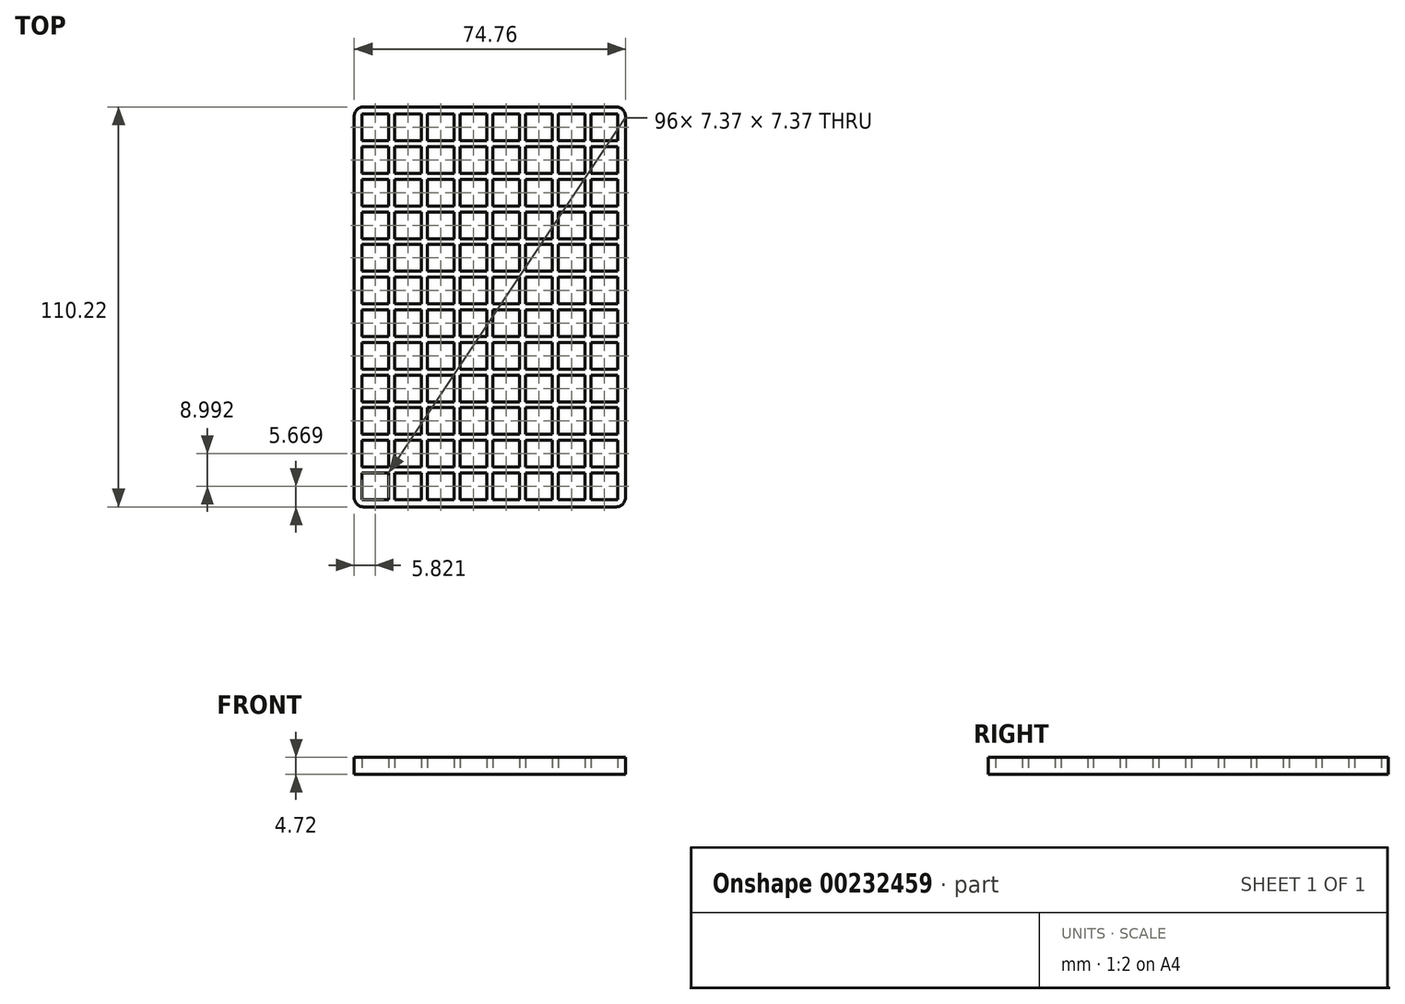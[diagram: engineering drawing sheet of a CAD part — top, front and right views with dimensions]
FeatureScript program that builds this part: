
annotation { "Feature Type Name" : "Feature", "Feature Type Description" : "" }
export const myFeature = defineFeature(function(context is Context, id is Id, definition is map)
    precondition{}
    {
        {
            var Q0;
            Q0=qCreatedBy(makeId("Top.planeOp"),FACE);
            var sketch = newSketch(context, id + "F0", { "sketchPlane" : qUnion([Q0])});
            skLineSegment(sketch, "E0.bottom", {"start": v(-37.38, 55.1) * mm, "end": v(37.38, 55.1) * mm});
            skLineSegment(sketch, "E0.top", {"start": v(-37.38, -55.1) * mm, "end": v(37.38, -55.1) * mm});
            skLineSegment(sketch, "E0.left", {"start": v(-37.38, 55.1) * mm, "end": v(-37.38, -55.1) * mm});
            skLineSegment(sketch, "E0.right", {"start": v(37.38, 55.1) * mm, "end": v(37.38, -55.1) * mm});
            skLineSegment(sketch, "E1.bottom", {"start": v(-35.24, 53.15) * mm, "end": v(-27.88, 53.15) * mm});
            skLineSegment(sketch, "E1.top", {"start": v(-35.24, 45.78) * mm, "end": v(-27.88, 45.78) * mm});
            skLineSegment(sketch, "E1.left", {"start": v(-35.24, 53.15) * mm, "end": v(-35.24, 45.78) * mm});
            skLineSegment(sketch, "E1.right", {"start": v(-27.88, 53.15) * mm, "end": v(-27.88, 45.78) * mm});
            skLineSegment(sketch, "E2.1.0.0", {"start": v(-18.86, 53.15) * mm, "end": v(-18.86, 45.78) * mm});
            skLineSegment(sketch, "E2.1.0.1", {"start": v(-26.23, 45.78) * mm, "end": v(-18.86, 45.78) * mm});
            skLineSegment(sketch, "E2.1.0.2", {"start": v(-26.23, 53.15) * mm, "end": v(-26.23, 45.78) * mm});
            skLineSegment(sketch, "E2.1.0.3", {"start": v(-26.23, 53.15) * mm, "end": v(-18.86, 53.15) * mm});
            skLineSegment(sketch, "E2.2.0.0", {"start": v(-9.84, 53.15) * mm, "end": v(-9.84, 45.78) * mm});
            skLineSegment(sketch, "E2.2.0.1", {"start": v(-17.2, 45.78) * mm, "end": v(-9.84, 45.78) * mm});
            skLineSegment(sketch, "E2.2.0.2", {"start": v(-17.2, 53.15) * mm, "end": v(-17.2, 45.78) * mm});
            skLineSegment(sketch, "E2.2.0.3", {"start": v(-17.2, 53.15) * mm, "end": v(-9.84, 53.15) * mm});
            skLineSegment(sketch, "E3.1.0.0", {"start": v(0.83, 53.15) * mm, "end": v(0.83, 45.78) * mm});
            skLineSegment(sketch, "E3.1.0.1", {"start": v(0.83, 45.78) * mm, "end": v(8.2, 45.78) * mm});
            skLineSegment(sketch, "E3.1.0.2", {"start": v(-0.83, 53.15) * mm, "end": v(-0.83, 45.78) * mm});
            skLineSegment(sketch, "E3.1.0.3", {"start": v(0.83, 53.15) * mm, "end": v(8.2, 53.15) * mm});
            skLineSegment(sketch, "E3.1.0.4", {"start": v(17.2, 53.15) * mm, "end": v(17.2, 45.78) * mm});
            skLineSegment(sketch, "E3.1.0.5", {"start": v(-8.2, 53.15) * mm, "end": v(-8.2, 45.78) * mm});
            skLineSegment(sketch, "E3.1.0.6", {"start": v(-8.2, 45.78) * mm, "end": v(-0.83, 45.78) * mm});
            skLineSegment(sketch, "E3.1.0.7", {"start": v(9.84, 53.15) * mm, "end": v(17.2, 53.15) * mm});
            skLineSegment(sketch, "E3.1.0.8", {"start": v(9.84, 45.78) * mm, "end": v(17.2, 45.78) * mm});
            skLineSegment(sketch, "E3.1.0.9", {"start": v(8.2, 53.15) * mm, "end": v(8.2, 45.78) * mm});
            skLineSegment(sketch, "E3.1.0.10", {"start": v(-8.2, 53.15) * mm, "end": v(-0.83, 53.15) * mm});
            skLineSegment(sketch, "E3.1.0.11", {"start": v(9.84, 53.15) * mm, "end": v(9.84, 45.78) * mm});
            skLineSegment(sketch, "E3.2.0.0", {"start": v(27.88, 53.15) * mm, "end": v(27.88, 45.78) * mm});
            skLineSegment(sketch, "E3.2.0.1", {"start": v(27.88, 45.78) * mm, "end": v(35.24, 45.78) * mm});
            skLineSegment(sketch, "E3.2.0.2", {"start": v(26.23, 53.15) * mm, "end": v(26.23, 45.78) * mm});
            skLineSegment(sketch, "E3.2.0.3", {"start": v(27.88, 53.15) * mm, "end": v(35.24, 53.15) * mm});
            skLineSegment(sketch, "E3.2.0.5", {"start": v(18.86, 53.15) * mm, "end": v(18.86, 45.78) * mm});
            skLineSegment(sketch, "E3.2.0.6", {"start": v(18.86, 45.78) * mm, "end": v(26.23, 45.78) * mm});
            skLineSegment(sketch, "E3.2.0.9", {"start": v(35.24, 53.15) * mm, "end": v(35.24, 45.78) * mm});
            skLineSegment(sketch, "E3.2.0.10", {"start": v(18.86, 53.15) * mm, "end": v(26.23, 53.15) * mm});
            skLineSegment(sketch, "E4.1.0.0", {"start": v(-8.2, 44.16) * mm, "end": v(-0.83, 44.16) * mm});
            skLineSegment(sketch, "E4.1.0.1", {"start": v(0.83, 44.16) * mm, "end": v(8.2, 44.16) * mm});
            skLineSegment(sketch, "E4.1.0.2", {"start": v(18.86, 44.16) * mm, "end": v(26.23, 44.16) * mm});
            skLineSegment(sketch, "E4.1.0.3", {"start": v(-17.2, 36.8) * mm, "end": v(-9.84, 36.8) * mm});
            skLineSegment(sketch, "E4.1.0.4", {"start": v(8.2, 44.16) * mm, "end": v(8.2, 36.8) * mm});
            skLineSegment(sketch, "E4.1.0.5", {"start": v(-35.24, 36.8) * mm, "end": v(-27.88, 36.8) * mm});
            skLineSegment(sketch, "E4.1.0.6", {"start": v(-17.2, 44.16) * mm, "end": v(-17.2, 36.8) * mm});
            skLineSegment(sketch, "E4.1.0.7", {"start": v(-17.2, 44.16) * mm, "end": v(-9.84, 44.16) * mm});
            skLineSegment(sketch, "E4.1.0.8", {"start": v(-0.83, 44.16) * mm, "end": v(-0.83, 36.8) * mm});
            skLineSegment(sketch, "E4.1.0.9", {"start": v(-35.24, 44.16) * mm, "end": v(-27.88, 44.16) * mm});
            skLineSegment(sketch, "E4.1.0.10", {"start": v(27.88, 44.16) * mm, "end": v(35.24, 44.16) * mm});
            skLineSegment(sketch, "E4.1.0.11", {"start": v(-8.2, 36.8) * mm, "end": v(-0.83, 36.8) * mm});
            skLineSegment(sketch, "E4.1.0.12", {"start": v(-35.24, 44.16) * mm, "end": v(-35.24, 36.8) * mm});
            skLineSegment(sketch, "E4.1.0.13", {"start": v(-27.88, 44.16) * mm, "end": v(-27.88, 36.8) * mm});
            skLineSegment(sketch, "E4.1.0.14", {"start": v(0.83, 36.8) * mm, "end": v(8.2, 36.8) * mm});
            skLineSegment(sketch, "E4.1.0.15", {"start": v(18.86, 36.8) * mm, "end": v(26.23, 36.8) * mm});
            skLineSegment(sketch, "E4.1.0.16", {"start": v(-18.86, 44.16) * mm, "end": v(-18.86, 36.8) * mm});
            skLineSegment(sketch, "E4.1.0.17", {"start": v(-26.23, 36.8) * mm, "end": v(-18.86, 36.8) * mm});
            skLineSegment(sketch, "E4.1.0.18", {"start": v(-26.23, 44.16) * mm, "end": v(-26.23, 36.8) * mm});
            skLineSegment(sketch, "E4.1.0.19", {"start": v(-26.23, 44.16) * mm, "end": v(-18.86, 44.16) * mm});
            skLineSegment(sketch, "E4.1.0.20", {"start": v(-9.84, 44.16) * mm, "end": v(-9.84, 36.8) * mm});
            skLineSegment(sketch, "E4.1.0.21", {"start": v(9.84, 44.16) * mm, "end": v(9.84, 36.8) * mm});
            skLineSegment(sketch, "E4.1.0.22", {"start": v(9.84, 44.16) * mm, "end": v(17.2, 44.16) * mm});
            skLineSegment(sketch, "E4.1.0.23", {"start": v(17.2, 44.16) * mm, "end": v(17.2, 36.8) * mm});
            skLineSegment(sketch, "E4.1.0.24", {"start": v(27.88, 36.8) * mm, "end": v(35.24, 36.8) * mm});
            skLineSegment(sketch, "E4.1.0.25", {"start": v(0.83, 44.16) * mm, "end": v(0.83, 36.8) * mm});
            skLineSegment(sketch, "E4.1.0.26", {"start": v(18.86, 44.16) * mm, "end": v(18.86, 36.8) * mm});
            skLineSegment(sketch, "E4.1.0.27", {"start": v(27.88, 44.16) * mm, "end": v(27.88, 36.8) * mm});
            skLineSegment(sketch, "E4.1.0.28", {"start": v(9.84, 36.8) * mm, "end": v(17.2, 36.8) * mm});
            skLineSegment(sketch, "E4.1.0.29", {"start": v(26.23, 44.16) * mm, "end": v(26.23, 36.8) * mm});
            skLineSegment(sketch, "E4.1.0.30", {"start": v(-8.2, 44.16) * mm, "end": v(-8.2, 36.8) * mm});
            skLineSegment(sketch, "E4.1.0.31", {"start": v(35.24, 44.16) * mm, "end": v(35.24, 36.8) * mm});
            skLineSegment(sketch, "E4.2.0.0", {"start": v(-8.2, 35.17) * mm, "end": v(-0.83, 35.17) * mm});
            skLineSegment(sketch, "E4.2.0.1", {"start": v(0.83, 35.17) * mm, "end": v(8.2, 35.17) * mm});
            skLineSegment(sketch, "E4.2.0.2", {"start": v(18.86, 35.17) * mm, "end": v(26.23, 35.17) * mm});
            skLineSegment(sketch, "E4.2.0.3", {"start": v(-17.2, 27.8) * mm, "end": v(-9.84, 27.8) * mm});
            skLineSegment(sketch, "E4.2.0.4", {"start": v(8.2, 35.17) * mm, "end": v(8.2, 27.8) * mm});
            skLineSegment(sketch, "E4.2.0.5", {"start": v(-35.24, 27.8) * mm, "end": v(-27.88, 27.8) * mm});
            skLineSegment(sketch, "E4.2.0.6", {"start": v(-17.2, 35.17) * mm, "end": v(-17.2, 27.8) * mm});
            skLineSegment(sketch, "E4.2.0.7", {"start": v(-17.2, 35.17) * mm, "end": v(-9.84, 35.17) * mm});
            skLineSegment(sketch, "E4.2.0.8", {"start": v(-0.83, 35.17) * mm, "end": v(-0.83, 27.8) * mm});
            skLineSegment(sketch, "E4.2.0.9", {"start": v(-35.24, 35.17) * mm, "end": v(-27.88, 35.17) * mm});
            skLineSegment(sketch, "E4.2.0.10", {"start": v(27.88, 35.17) * mm, "end": v(35.24, 35.17) * mm});
            skLineSegment(sketch, "E4.2.0.11", {"start": v(-8.2, 27.8) * mm, "end": v(-0.83, 27.8) * mm});
            skLineSegment(sketch, "E4.2.0.12", {"start": v(-35.24, 35.17) * mm, "end": v(-35.24, 27.8) * mm});
            skLineSegment(sketch, "E4.2.0.13", {"start": v(-27.88, 35.17) * mm, "end": v(-27.88, 27.8) * mm});
            skLineSegment(sketch, "E4.2.0.14", {"start": v(0.83, 27.8) * mm, "end": v(8.2, 27.8) * mm});
            skLineSegment(sketch, "E4.2.0.15", {"start": v(18.86, 27.8) * mm, "end": v(26.23, 27.8) * mm});
            skLineSegment(sketch, "E4.2.0.16", {"start": v(-18.86, 35.17) * mm, "end": v(-18.86, 27.8) * mm});
            skLineSegment(sketch, "E4.2.0.17", {"start": v(-26.23, 27.8) * mm, "end": v(-18.86, 27.8) * mm});
            skLineSegment(sketch, "E4.2.0.18", {"start": v(-26.23, 35.17) * mm, "end": v(-26.23, 27.8) * mm});
            skLineSegment(sketch, "E4.2.0.19", {"start": v(-26.23, 35.17) * mm, "end": v(-18.86, 35.17) * mm});
            skLineSegment(sketch, "E4.2.0.20", {"start": v(-9.84, 35.17) * mm, "end": v(-9.84, 27.8) * mm});
            skLineSegment(sketch, "E4.2.0.21", {"start": v(9.84, 35.17) * mm, "end": v(9.84, 27.8) * mm});
            skLineSegment(sketch, "E4.2.0.22", {"start": v(9.84, 35.17) * mm, "end": v(17.2, 35.17) * mm});
            skLineSegment(sketch, "E4.2.0.23", {"start": v(17.2, 35.17) * mm, "end": v(17.2, 27.8) * mm});
            skLineSegment(sketch, "E4.2.0.24", {"start": v(27.88, 27.8) * mm, "end": v(35.24, 27.8) * mm});
            skLineSegment(sketch, "E4.2.0.25", {"start": v(0.83, 35.17) * mm, "end": v(0.83, 27.8) * mm});
            skLineSegment(sketch, "E4.2.0.26", {"start": v(18.86, 35.17) * mm, "end": v(18.86, 27.8) * mm});
            skLineSegment(sketch, "E4.2.0.27", {"start": v(27.88, 35.17) * mm, "end": v(27.88, 27.8) * mm});
            skLineSegment(sketch, "E4.2.0.28", {"start": v(9.84, 27.8) * mm, "end": v(17.2, 27.8) * mm});
            skLineSegment(sketch, "E4.2.0.29", {"start": v(26.23, 35.17) * mm, "end": v(26.23, 27.8) * mm});
            skLineSegment(sketch, "E4.2.0.30", {"start": v(-8.2, 35.17) * mm, "end": v(-8.2, 27.8) * mm});
            skLineSegment(sketch, "E4.2.0.31", {"start": v(35.24, 35.17) * mm, "end": v(35.24, 27.8) * mm});
            skLineSegment(sketch, "E4.direction1", {"start": v(-35.24, 45.78) * mm, "end": v(-35.24, 36.8) * mm, "construction": true});
            skLineSegment(sketch, "E5.0.3.0", {"start": v(-8.2, 26.17) * mm, "end": v(-0.83, 26.17) * mm});
            skLineSegment(sketch, "E5.3.3.0", {"start": v(0.83, 26.17) * mm, "end": v(8.2, 26.17) * mm});
            skLineSegment(sketch, "E5.6.3.0", {"start": v(18.86, 26.17) * mm, "end": v(26.23, 26.17) * mm});
            skLineSegment(sketch, "E5.9.3.0", {"start": v(-17.2, 18.8) * mm, "end": v(-9.84, 18.8) * mm});
            skLineSegment(sketch, "E5.12.3.0", {"start": v(8.2, 26.17) * mm, "end": v(8.2, 18.8) * mm});
            skLineSegment(sketch, "E5.15.3.0", {"start": v(-35.24, 18.8) * mm, "end": v(-27.88, 18.8) * mm});
            skLineSegment(sketch, "E5.18.3.0", {"start": v(-17.2, 26.17) * mm, "end": v(-17.2, 18.8) * mm});
            skLineSegment(sketch, "E5.21.3.0", {"start": v(-17.2, 26.17) * mm, "end": v(-9.84, 26.17) * mm});
            skLineSegment(sketch, "E5.24.3.0", {"start": v(-0.83, 26.17) * mm, "end": v(-0.83, 18.8) * mm});
            skLineSegment(sketch, "E5.27.3.0", {"start": v(-35.24, 26.17) * mm, "end": v(-27.88, 26.17) * mm});
            skLineSegment(sketch, "E5.30.3.0", {"start": v(27.88, 26.17) * mm, "end": v(35.24, 26.17) * mm});
            skLineSegment(sketch, "E5.33.3.0", {"start": v(-8.2, 18.8) * mm, "end": v(-0.83, 18.8) * mm});
            skLineSegment(sketch, "E5.36.3.0", {"start": v(-35.24, 26.17) * mm, "end": v(-35.24, 18.8) * mm});
            skLineSegment(sketch, "E5.39.3.0", {"start": v(-27.88, 26.17) * mm, "end": v(-27.88, 18.8) * mm});
            skLineSegment(sketch, "E5.42.3.0", {"start": v(0.83, 18.8) * mm, "end": v(8.2, 18.8) * mm});
            skLineSegment(sketch, "E5.45.3.0", {"start": v(18.86, 18.8) * mm, "end": v(26.23, 18.8) * mm});
            skLineSegment(sketch, "E5.48.3.0", {"start": v(-18.86, 26.17) * mm, "end": v(-18.86, 18.8) * mm});
            skLineSegment(sketch, "E5.51.3.0", {"start": v(-26.23, 18.8) * mm, "end": v(-18.86, 18.8) * mm});
            skLineSegment(sketch, "E5.54.3.0", {"start": v(-26.23, 26.17) * mm, "end": v(-26.23, 18.8) * mm});
            skLineSegment(sketch, "E5.57.3.0", {"start": v(-26.23, 26.17) * mm, "end": v(-18.86, 26.17) * mm});
            skLineSegment(sketch, "E5.60.3.0", {"start": v(-9.84, 26.17) * mm, "end": v(-9.84, 18.8) * mm});
            skLineSegment(sketch, "E5.63.3.0", {"start": v(9.84, 26.17) * mm, "end": v(9.84, 18.8) * mm});
            skLineSegment(sketch, "E5.66.3.0", {"start": v(9.84, 26.17) * mm, "end": v(17.2, 26.17) * mm});
            skLineSegment(sketch, "E5.69.3.0", {"start": v(17.2, 26.17) * mm, "end": v(17.2, 18.8) * mm});
            skLineSegment(sketch, "E5.72.3.0", {"start": v(27.88, 18.8) * mm, "end": v(35.24, 18.8) * mm});
            skLineSegment(sketch, "E5.75.3.0", {"start": v(0.83, 26.17) * mm, "end": v(0.83, 18.8) * mm});
            skLineSegment(sketch, "E5.78.3.0", {"start": v(18.86, 26.17) * mm, "end": v(18.86, 18.8) * mm});
            skLineSegment(sketch, "E5.81.3.0", {"start": v(27.88, 26.17) * mm, "end": v(27.88, 18.8) * mm});
            skLineSegment(sketch, "E5.84.3.0", {"start": v(9.84, 18.8) * mm, "end": v(17.2, 18.8) * mm});
            skLineSegment(sketch, "E5.87.3.0", {"start": v(26.23, 26.17) * mm, "end": v(26.23, 18.8) * mm});
            skLineSegment(sketch, "E5.90.3.0", {"start": v(-8.2, 26.17) * mm, "end": v(-8.2, 18.8) * mm});
            skLineSegment(sketch, "E5.93.3.0", {"start": v(35.24, 26.17) * mm, "end": v(35.24, 18.8) * mm});
            skLineSegment(sketch, "E5.0.4.0", {"start": v(-8.2, 17.18) * mm, "end": v(-0.83, 17.18) * mm});
            skLineSegment(sketch, "E5.3.4.0", {"start": v(0.83, 17.18) * mm, "end": v(8.2, 17.18) * mm});
            skLineSegment(sketch, "E5.6.4.0", {"start": v(18.86, 17.18) * mm, "end": v(26.23, 17.18) * mm});
            skLineSegment(sketch, "E5.9.4.0", {"start": v(-17.2, 9.82) * mm, "end": v(-9.84, 9.82) * mm});
            skLineSegment(sketch, "E5.12.4.0", {"start": v(8.2, 17.18) * mm, "end": v(8.2, 9.82) * mm});
            skLineSegment(sketch, "E5.15.4.0", {"start": v(-35.24, 9.82) * mm, "end": v(-27.88, 9.82) * mm});
            skLineSegment(sketch, "E5.18.4.0", {"start": v(-17.2, 17.18) * mm, "end": v(-17.2, 9.82) * mm});
            skLineSegment(sketch, "E5.21.4.0", {"start": v(-17.2, 17.18) * mm, "end": v(-9.84, 17.18) * mm});
            skLineSegment(sketch, "E5.24.4.0", {"start": v(-0.83, 17.18) * mm, "end": v(-0.83, 9.82) * mm});
            skLineSegment(sketch, "E5.27.4.0", {"start": v(-35.24, 17.18) * mm, "end": v(-27.88, 17.18) * mm});
            skLineSegment(sketch, "E5.30.4.0", {"start": v(27.88, 17.18) * mm, "end": v(35.24, 17.18) * mm});
            skLineSegment(sketch, "E5.33.4.0", {"start": v(-8.2, 9.82) * mm, "end": v(-0.83, 9.82) * mm});
            skLineSegment(sketch, "E5.36.4.0", {"start": v(-35.24, 17.18) * mm, "end": v(-35.24, 9.82) * mm});
            skLineSegment(sketch, "E5.39.4.0", {"start": v(-27.88, 17.18) * mm, "end": v(-27.88, 9.82) * mm});
            skLineSegment(sketch, "E5.42.4.0", {"start": v(0.83, 9.82) * mm, "end": v(8.2, 9.82) * mm});
            skLineSegment(sketch, "E5.45.4.0", {"start": v(18.86, 9.82) * mm, "end": v(26.23, 9.82) * mm});
            skLineSegment(sketch, "E5.48.4.0", {"start": v(-18.86, 17.18) * mm, "end": v(-18.86, 9.82) * mm});
            skLineSegment(sketch, "E5.51.4.0", {"start": v(-26.23, 9.82) * mm, "end": v(-18.86, 9.82) * mm});
            skLineSegment(sketch, "E5.54.4.0", {"start": v(-26.23, 17.18) * mm, "end": v(-26.23, 9.82) * mm});
            skLineSegment(sketch, "E5.57.4.0", {"start": v(-26.23, 17.18) * mm, "end": v(-18.86, 17.18) * mm});
            skLineSegment(sketch, "E5.60.4.0", {"start": v(-9.84, 17.18) * mm, "end": v(-9.84, 9.82) * mm});
            skLineSegment(sketch, "E5.63.4.0", {"start": v(9.84, 17.18) * mm, "end": v(9.84, 9.82) * mm});
            skLineSegment(sketch, "E5.66.4.0", {"start": v(9.84, 17.18) * mm, "end": v(17.2, 17.18) * mm});
            skLineSegment(sketch, "E5.69.4.0", {"start": v(17.2, 17.18) * mm, "end": v(17.2, 9.82) * mm});
            skLineSegment(sketch, "E5.72.4.0", {"start": v(27.88, 9.82) * mm, "end": v(35.24, 9.82) * mm});
            skLineSegment(sketch, "E5.75.4.0", {"start": v(0.83, 17.18) * mm, "end": v(0.83, 9.82) * mm});
            skLineSegment(sketch, "E5.78.4.0", {"start": v(18.86, 17.18) * mm, "end": v(18.86, 9.82) * mm});
            skLineSegment(sketch, "E5.81.4.0", {"start": v(27.88, 17.18) * mm, "end": v(27.88, 9.82) * mm});
            skLineSegment(sketch, "E5.84.4.0", {"start": v(9.84, 9.82) * mm, "end": v(17.2, 9.82) * mm});
            skLineSegment(sketch, "E5.87.4.0", {"start": v(26.23, 17.18) * mm, "end": v(26.23, 9.82) * mm});
            skLineSegment(sketch, "E5.90.4.0", {"start": v(-8.2, 17.18) * mm, "end": v(-8.2, 9.82) * mm});
            skLineSegment(sketch, "E5.93.4.0", {"start": v(35.24, 17.18) * mm, "end": v(35.24, 9.82) * mm});
            skLineSegment(sketch, "E5.0.5.0", {"start": v(-8.2, 8.2) * mm, "end": v(-0.83, 8.2) * mm});
            skLineSegment(sketch, "E5.3.5.0", {"start": v(0.83, 8.2) * mm, "end": v(8.2, 8.2) * mm});
            skLineSegment(sketch, "E5.6.5.0", {"start": v(18.86, 8.2) * mm, "end": v(26.23, 8.2) * mm});
            skLineSegment(sketch, "E5.9.5.0", {"start": v(-17.2, 0.83) * mm, "end": v(-9.84, 0.83) * mm});
            skLineSegment(sketch, "E5.12.5.0", {"start": v(8.2, 8.2) * mm, "end": v(8.2, 0.83) * mm});
            skLineSegment(sketch, "E5.15.5.0", {"start": v(-35.24, 0.83) * mm, "end": v(-27.88, 0.83) * mm});
            skLineSegment(sketch, "E5.18.5.0", {"start": v(-17.2, 8.2) * mm, "end": v(-17.2, 0.83) * mm});
            skLineSegment(sketch, "E5.21.5.0", {"start": v(-17.2, 8.2) * mm, "end": v(-9.84, 8.2) * mm});
            skLineSegment(sketch, "E5.24.5.0", {"start": v(-0.83, 8.2) * mm, "end": v(-0.83, 0.83) * mm});
            skLineSegment(sketch, "E5.27.5.0", {"start": v(-35.24, 8.2) * mm, "end": v(-27.88, 8.2) * mm});
            skLineSegment(sketch, "E5.30.5.0", {"start": v(27.88, 8.2) * mm, "end": v(35.24, 8.2) * mm});
            skLineSegment(sketch, "E5.33.5.0", {"start": v(-8.2, 0.83) * mm, "end": v(-0.83, 0.83) * mm});
            skLineSegment(sketch, "E5.36.5.0", {"start": v(-35.24, 8.2) * mm, "end": v(-35.24, 0.83) * mm});
            skLineSegment(sketch, "E5.39.5.0", {"start": v(-27.88, 8.2) * mm, "end": v(-27.88, 0.83) * mm});
            skLineSegment(sketch, "E5.42.5.0", {"start": v(0.83, 0.83) * mm, "end": v(8.2, 0.83) * mm});
            skLineSegment(sketch, "E5.45.5.0", {"start": v(18.86, 0.83) * mm, "end": v(26.23, 0.83) * mm});
            skLineSegment(sketch, "E5.48.5.0", {"start": v(-18.86, 8.2) * mm, "end": v(-18.86, 0.83) * mm});
            skLineSegment(sketch, "E5.51.5.0", {"start": v(-26.23, 0.83) * mm, "end": v(-18.86, 0.83) * mm});
            skLineSegment(sketch, "E5.54.5.0", {"start": v(-26.23, 8.2) * mm, "end": v(-26.23, 0.83) * mm});
            skLineSegment(sketch, "E5.57.5.0", {"start": v(-26.23, 8.2) * mm, "end": v(-18.86, 8.2) * mm});
            skLineSegment(sketch, "E5.60.5.0", {"start": v(-9.84, 8.2) * mm, "end": v(-9.84, 0.83) * mm});
            skLineSegment(sketch, "E5.63.5.0", {"start": v(9.84, 8.2) * mm, "end": v(9.84, 0.83) * mm});
            skLineSegment(sketch, "E5.66.5.0", {"start": v(9.84, 8.2) * mm, "end": v(17.2, 8.2) * mm});
            skLineSegment(sketch, "E5.69.5.0", {"start": v(17.2, 8.2) * mm, "end": v(17.2, 0.83) * mm});
            skLineSegment(sketch, "E5.72.5.0", {"start": v(27.88, 0.83) * mm, "end": v(35.24, 0.83) * mm});
            skLineSegment(sketch, "E5.75.5.0", {"start": v(0.83, 8.2) * mm, "end": v(0.83, 0.83) * mm});
            skLineSegment(sketch, "E5.78.5.0", {"start": v(18.86, 8.2) * mm, "end": v(18.86, 0.83) * mm});
            skLineSegment(sketch, "E5.81.5.0", {"start": v(27.88, 8.2) * mm, "end": v(27.88, 0.83) * mm});
            skLineSegment(sketch, "E5.84.5.0", {"start": v(9.84, 0.83) * mm, "end": v(17.2, 0.83) * mm});
            skLineSegment(sketch, "E5.87.5.0", {"start": v(26.23, 8.2) * mm, "end": v(26.23, 0.83) * mm});
            skLineSegment(sketch, "E5.90.5.0", {"start": v(-8.2, 8.2) * mm, "end": v(-8.2, 0.83) * mm});
            skLineSegment(sketch, "E5.93.5.0", {"start": v(35.24, 8.2) * mm, "end": v(35.24, 0.83) * mm});
            skLineSegment(sketch, "E5.0.6.0", {"start": v(-8.2, -0.8) * mm, "end": v(-0.83, -0.8) * mm});
            skLineSegment(sketch, "E5.3.6.0", {"start": v(0.83, -0.8) * mm, "end": v(8.2, -0.8) * mm});
            skLineSegment(sketch, "E5.6.6.0", {"start": v(18.86, -0.8) * mm, "end": v(26.23, -0.8) * mm});
            skLineSegment(sketch, "E5.9.6.0", {"start": v(-17.2, -8.17) * mm, "end": v(-9.84, -8.17) * mm});
            skLineSegment(sketch, "E5.12.6.0", {"start": v(8.2, -0.8) * mm, "end": v(8.2, -8.17) * mm});
            skLineSegment(sketch, "E5.15.6.0", {"start": v(-35.24, -8.17) * mm, "end": v(-27.88, -8.17) * mm});
            skLineSegment(sketch, "E5.18.6.0", {"start": v(-17.2, -0.8) * mm, "end": v(-17.2, -8.17) * mm});
            skLineSegment(sketch, "E5.21.6.0", {"start": v(-17.2, -0.8) * mm, "end": v(-9.84, -0.8) * mm});
            skLineSegment(sketch, "E5.24.6.0", {"start": v(-0.83, -0.8) * mm, "end": v(-0.83, -8.17) * mm});
            skLineSegment(sketch, "E5.27.6.0", {"start": v(-35.24, -0.8) * mm, "end": v(-27.88, -0.8) * mm});
            skLineSegment(sketch, "E5.30.6.0", {"start": v(27.88, -0.8) * mm, "end": v(35.24, -0.8) * mm});
            skLineSegment(sketch, "E5.33.6.0", {"start": v(-8.2, -8.17) * mm, "end": v(-0.83, -8.17) * mm});
            skLineSegment(sketch, "E5.36.6.0", {"start": v(-35.24, -0.8) * mm, "end": v(-35.24, -8.17) * mm});
            skLineSegment(sketch, "E5.39.6.0", {"start": v(-27.88, -0.8) * mm, "end": v(-27.88, -8.17) * mm});
            skLineSegment(sketch, "E5.42.6.0", {"start": v(0.83, -8.17) * mm, "end": v(8.2, -8.17) * mm});
            skLineSegment(sketch, "E5.45.6.0", {"start": v(18.86, -8.17) * mm, "end": v(26.23, -8.17) * mm});
            skLineSegment(sketch, "E5.48.6.0", {"start": v(-18.86, -0.8) * mm, "end": v(-18.86, -8.17) * mm});
            skLineSegment(sketch, "E5.51.6.0", {"start": v(-26.23, -8.17) * mm, "end": v(-18.86, -8.17) * mm});
            skLineSegment(sketch, "E5.54.6.0", {"start": v(-26.23, -0.8) * mm, "end": v(-26.23, -8.17) * mm});
            skLineSegment(sketch, "E5.57.6.0", {"start": v(-26.23, -0.8) * mm, "end": v(-18.86, -0.8) * mm});
            skLineSegment(sketch, "E5.60.6.0", {"start": v(-9.84, -0.8) * mm, "end": v(-9.84, -8.17) * mm});
            skLineSegment(sketch, "E5.63.6.0", {"start": v(9.84, -0.8) * mm, "end": v(9.84, -8.17) * mm});
            skLineSegment(sketch, "E5.66.6.0", {"start": v(9.84, -0.8) * mm, "end": v(17.2, -0.8) * mm});
            skLineSegment(sketch, "E5.69.6.0", {"start": v(17.2, -0.8) * mm, "end": v(17.2, -8.17) * mm});
            skLineSegment(sketch, "E5.72.6.0", {"start": v(27.88, -8.17) * mm, "end": v(35.24, -8.17) * mm});
            skLineSegment(sketch, "E5.75.6.0", {"start": v(0.83, -0.8) * mm, "end": v(0.83, -8.17) * mm});
            skLineSegment(sketch, "E5.78.6.0", {"start": v(18.86, -0.8) * mm, "end": v(18.86, -8.17) * mm});
            skLineSegment(sketch, "E5.81.6.0", {"start": v(27.88, -0.8) * mm, "end": v(27.88, -8.17) * mm});
            skLineSegment(sketch, "E5.84.6.0", {"start": v(9.84, -8.17) * mm, "end": v(17.2, -8.17) * mm});
            skLineSegment(sketch, "E5.87.6.0", {"start": v(26.23, -0.8) * mm, "end": v(26.23, -8.17) * mm});
            skLineSegment(sketch, "E5.90.6.0", {"start": v(-8.2, -0.8) * mm, "end": v(-8.2, -8.17) * mm});
            skLineSegment(sketch, "E5.93.6.0", {"start": v(35.24, -0.8) * mm, "end": v(35.24, -8.17) * mm});
            skLineSegment(sketch, "E5.0.7.0", {"start": v(-8.2, -9.8) * mm, "end": v(-0.83, -9.8) * mm});
            skLineSegment(sketch, "E5.3.7.0", {"start": v(0.83, -9.8) * mm, "end": v(8.2, -9.8) * mm});
            skLineSegment(sketch, "E5.6.7.0", {"start": v(18.86, -9.8) * mm, "end": v(26.23, -9.8) * mm});
            skLineSegment(sketch, "E5.9.7.0", {"start": v(-17.2, -17.16) * mm, "end": v(-9.84, -17.16) * mm});
            skLineSegment(sketch, "E5.12.7.0", {"start": v(8.2, -9.8) * mm, "end": v(8.2, -17.16) * mm});
            skLineSegment(sketch, "E5.15.7.0", {"start": v(-35.24, -17.16) * mm, "end": v(-27.88, -17.16) * mm});
            skLineSegment(sketch, "E5.18.7.0", {"start": v(-17.2, -9.8) * mm, "end": v(-17.2, -17.16) * mm});
            skLineSegment(sketch, "E5.21.7.0", {"start": v(-17.2, -9.8) * mm, "end": v(-9.84, -9.8) * mm});
            skLineSegment(sketch, "E5.24.7.0", {"start": v(-0.83, -9.8) * mm, "end": v(-0.83, -17.16) * mm});
            skLineSegment(sketch, "E5.27.7.0", {"start": v(-35.24, -9.8) * mm, "end": v(-27.88, -9.8) * mm});
            skLineSegment(sketch, "E5.30.7.0", {"start": v(27.88, -9.8) * mm, "end": v(35.24, -9.8) * mm});
            skLineSegment(sketch, "E5.33.7.0", {"start": v(-8.2, -17.16) * mm, "end": v(-0.83, -17.16) * mm});
            skLineSegment(sketch, "E5.36.7.0", {"start": v(-35.24, -9.8) * mm, "end": v(-35.24, -17.16) * mm});
            skLineSegment(sketch, "E5.39.7.0", {"start": v(-27.88, -9.8) * mm, "end": v(-27.88, -17.16) * mm});
            skLineSegment(sketch, "E5.42.7.0", {"start": v(0.83, -17.16) * mm, "end": v(8.2, -17.16) * mm});
            skLineSegment(sketch, "E5.45.7.0", {"start": v(18.86, -17.16) * mm, "end": v(26.23, -17.16) * mm});
            skLineSegment(sketch, "E5.48.7.0", {"start": v(-18.86, -9.8) * mm, "end": v(-18.86, -17.16) * mm});
            skLineSegment(sketch, "E5.51.7.0", {"start": v(-26.23, -17.16) * mm, "end": v(-18.86, -17.16) * mm});
            skLineSegment(sketch, "E5.54.7.0", {"start": v(-26.23, -9.8) * mm, "end": v(-26.23, -17.16) * mm});
            skLineSegment(sketch, "E5.57.7.0", {"start": v(-26.23, -9.8) * mm, "end": v(-18.86, -9.8) * mm});
            skLineSegment(sketch, "E5.60.7.0", {"start": v(-9.84, -9.8) * mm, "end": v(-9.84, -17.16) * mm});
            skLineSegment(sketch, "E5.63.7.0", {"start": v(9.84, -9.8) * mm, "end": v(9.84, -17.16) * mm});
            skLineSegment(sketch, "E5.66.7.0", {"start": v(9.84, -9.8) * mm, "end": v(17.2, -9.8) * mm});
            skLineSegment(sketch, "E5.69.7.0", {"start": v(17.2, -9.8) * mm, "end": v(17.2, -17.16) * mm});
            skLineSegment(sketch, "E5.72.7.0", {"start": v(27.88, -17.16) * mm, "end": v(35.24, -17.16) * mm});
            skLineSegment(sketch, "E5.75.7.0", {"start": v(0.83, -9.8) * mm, "end": v(0.83, -17.16) * mm});
            skLineSegment(sketch, "E5.78.7.0", {"start": v(18.86, -9.8) * mm, "end": v(18.86, -17.16) * mm});
            skLineSegment(sketch, "E5.81.7.0", {"start": v(27.88, -9.8) * mm, "end": v(27.88, -17.16) * mm});
            skLineSegment(sketch, "E5.84.7.0", {"start": v(9.84, -17.16) * mm, "end": v(17.2, -17.16) * mm});
            skLineSegment(sketch, "E5.87.7.0", {"start": v(26.23, -9.8) * mm, "end": v(26.23, -17.16) * mm});
            skLineSegment(sketch, "E5.90.7.0", {"start": v(-8.2, -9.8) * mm, "end": v(-8.2, -17.16) * mm});
            skLineSegment(sketch, "E5.93.7.0", {"start": v(35.24, -9.8) * mm, "end": v(35.24, -17.16) * mm});
            skLineSegment(sketch, "E5.0.8.0", {"start": v(-8.2, -18.78) * mm, "end": v(-0.83, -18.78) * mm});
            skLineSegment(sketch, "E5.3.8.0", {"start": v(0.83, -18.78) * mm, "end": v(8.2, -18.78) * mm});
            skLineSegment(sketch, "E5.6.8.0", {"start": v(18.86, -18.78) * mm, "end": v(26.23, -18.78) * mm});
            skLineSegment(sketch, "E5.9.8.0", {"start": v(-17.2, -26.15) * mm, "end": v(-9.84, -26.15) * mm});
            skLineSegment(sketch, "E5.12.8.0", {"start": v(8.2, -18.78) * mm, "end": v(8.2, -26.15) * mm});
            skLineSegment(sketch, "E5.15.8.0", {"start": v(-35.24, -26.15) * mm, "end": v(-27.88, -26.15) * mm});
            skLineSegment(sketch, "E5.18.8.0", {"start": v(-17.2, -18.78) * mm, "end": v(-17.2, -26.15) * mm});
            skLineSegment(sketch, "E5.21.8.0", {"start": v(-17.2, -18.78) * mm, "end": v(-9.84, -18.78) * mm});
            skLineSegment(sketch, "E5.24.8.0", {"start": v(-0.83, -18.78) * mm, "end": v(-0.83, -26.15) * mm});
            skLineSegment(sketch, "E5.27.8.0", {"start": v(-35.24, -18.78) * mm, "end": v(-27.88, -18.78) * mm});
            skLineSegment(sketch, "E5.30.8.0", {"start": v(27.88, -18.78) * mm, "end": v(35.24, -18.78) * mm});
            skLineSegment(sketch, "E5.33.8.0", {"start": v(-8.2, -26.15) * mm, "end": v(-0.83, -26.15) * mm});
            skLineSegment(sketch, "E5.36.8.0", {"start": v(-35.24, -18.78) * mm, "end": v(-35.24, -26.15) * mm});
            skLineSegment(sketch, "E5.39.8.0", {"start": v(-27.88, -18.78) * mm, "end": v(-27.88, -26.15) * mm});
            skLineSegment(sketch, "E5.42.8.0", {"start": v(0.83, -26.15) * mm, "end": v(8.2, -26.15) * mm});
            skLineSegment(sketch, "E5.45.8.0", {"start": v(18.86, -26.15) * mm, "end": v(26.23, -26.15) * mm});
            skLineSegment(sketch, "E5.48.8.0", {"start": v(-18.86, -18.78) * mm, "end": v(-18.86, -26.15) * mm});
            skLineSegment(sketch, "E5.51.8.0", {"start": v(-26.23, -26.15) * mm, "end": v(-18.86, -26.15) * mm});
            skLineSegment(sketch, "E5.54.8.0", {"start": v(-26.23, -18.78) * mm, "end": v(-26.23, -26.15) * mm});
            skLineSegment(sketch, "E5.57.8.0", {"start": v(-26.23, -18.78) * mm, "end": v(-18.86, -18.78) * mm});
            skLineSegment(sketch, "E5.60.8.0", {"start": v(-9.84, -18.78) * mm, "end": v(-9.84, -26.15) * mm});
            skLineSegment(sketch, "E5.63.8.0", {"start": v(9.84, -18.78) * mm, "end": v(9.84, -26.15) * mm});
            skLineSegment(sketch, "E5.66.8.0", {"start": v(9.84, -18.78) * mm, "end": v(17.2, -18.78) * mm});
            skLineSegment(sketch, "E5.69.8.0", {"start": v(17.2, -18.78) * mm, "end": v(17.2, -26.15) * mm});
            skLineSegment(sketch, "E5.72.8.0", {"start": v(27.88, -26.15) * mm, "end": v(35.24, -26.15) * mm});
            skLineSegment(sketch, "E5.75.8.0", {"start": v(0.83, -18.78) * mm, "end": v(0.83, -26.15) * mm});
            skLineSegment(sketch, "E5.78.8.0", {"start": v(18.86, -18.78) * mm, "end": v(18.86, -26.15) * mm});
            skLineSegment(sketch, "E5.81.8.0", {"start": v(27.88, -18.78) * mm, "end": v(27.88, -26.15) * mm});
            skLineSegment(sketch, "E5.84.8.0", {"start": v(9.84, -26.15) * mm, "end": v(17.2, -26.15) * mm});
            skLineSegment(sketch, "E5.87.8.0", {"start": v(26.23, -18.78) * mm, "end": v(26.23, -26.15) * mm});
            skLineSegment(sketch, "E5.90.8.0", {"start": v(-8.2, -18.78) * mm, "end": v(-8.2, -26.15) * mm});
            skLineSegment(sketch, "E5.93.8.0", {"start": v(35.24, -18.78) * mm, "end": v(35.24, -26.15) * mm});
            skLineSegment(sketch, "E5.0.9.0", {"start": v(-8.2, -27.77) * mm, "end": v(-0.83, -27.77) * mm});
            skLineSegment(sketch, "E5.3.9.0", {"start": v(0.83, -27.77) * mm, "end": v(8.2, -27.77) * mm});
            skLineSegment(sketch, "E5.6.9.0", {"start": v(18.86, -27.77) * mm, "end": v(26.23, -27.77) * mm});
            skLineSegment(sketch, "E5.9.9.0", {"start": v(-17.2, -35.14) * mm, "end": v(-9.84, -35.14) * mm});
            skLineSegment(sketch, "E5.12.9.0", {"start": v(8.2, -27.77) * mm, "end": v(8.2, -35.14) * mm});
            skLineSegment(sketch, "E5.15.9.0", {"start": v(-35.24, -35.14) * mm, "end": v(-27.88, -35.14) * mm});
            skLineSegment(sketch, "E5.18.9.0", {"start": v(-17.2, -27.77) * mm, "end": v(-17.2, -35.14) * mm});
            skLineSegment(sketch, "E5.21.9.0", {"start": v(-17.2, -27.77) * mm, "end": v(-9.84, -27.77) * mm});
            skLineSegment(sketch, "E5.24.9.0", {"start": v(-0.83, -27.77) * mm, "end": v(-0.83, -35.14) * mm});
            skLineSegment(sketch, "E5.27.9.0", {"start": v(-35.24, -27.77) * mm, "end": v(-27.88, -27.77) * mm});
            skLineSegment(sketch, "E5.30.9.0", {"start": v(27.88, -27.77) * mm, "end": v(35.24, -27.77) * mm});
            skLineSegment(sketch, "E5.33.9.0", {"start": v(-8.2, -35.14) * mm, "end": v(-0.83, -35.14) * mm});
            skLineSegment(sketch, "E5.36.9.0", {"start": v(-35.24, -27.77) * mm, "end": v(-35.24, -35.14) * mm});
            skLineSegment(sketch, "E5.39.9.0", {"start": v(-27.88, -27.77) * mm, "end": v(-27.88, -35.14) * mm});
            skLineSegment(sketch, "E5.42.9.0", {"start": v(0.83, -35.14) * mm, "end": v(8.2, -35.14) * mm});
            skLineSegment(sketch, "E5.45.9.0", {"start": v(18.86, -35.14) * mm, "end": v(26.23, -35.14) * mm});
            skLineSegment(sketch, "E5.48.9.0", {"start": v(-18.86, -27.77) * mm, "end": v(-18.86, -35.14) * mm});
            skLineSegment(sketch, "E5.51.9.0", {"start": v(-26.23, -35.14) * mm, "end": v(-18.86, -35.14) * mm});
            skLineSegment(sketch, "E5.54.9.0", {"start": v(-26.23, -27.77) * mm, "end": v(-26.23, -35.14) * mm});
            skLineSegment(sketch, "E5.57.9.0", {"start": v(-26.23, -27.77) * mm, "end": v(-18.86, -27.77) * mm});
            skLineSegment(sketch, "E5.60.9.0", {"start": v(-9.84, -27.77) * mm, "end": v(-9.84, -35.14) * mm});
            skLineSegment(sketch, "E5.63.9.0", {"start": v(9.84, -27.77) * mm, "end": v(9.84, -35.14) * mm});
            skLineSegment(sketch, "E5.66.9.0", {"start": v(9.84, -27.77) * mm, "end": v(17.2, -27.77) * mm});
            skLineSegment(sketch, "E5.69.9.0", {"start": v(17.2, -27.77) * mm, "end": v(17.2, -35.14) * mm});
            skLineSegment(sketch, "E5.72.9.0", {"start": v(27.88, -35.14) * mm, "end": v(35.24, -35.14) * mm});
            skLineSegment(sketch, "E5.75.9.0", {"start": v(0.83, -27.77) * mm, "end": v(0.83, -35.14) * mm});
            skLineSegment(sketch, "E5.78.9.0", {"start": v(18.86, -27.77) * mm, "end": v(18.86, -35.14) * mm});
            skLineSegment(sketch, "E5.81.9.0", {"start": v(27.88, -27.77) * mm, "end": v(27.88, -35.14) * mm});
            skLineSegment(sketch, "E5.84.9.0", {"start": v(9.84, -35.14) * mm, "end": v(17.2, -35.14) * mm});
            skLineSegment(sketch, "E5.87.9.0", {"start": v(26.23, -27.77) * mm, "end": v(26.23, -35.14) * mm});
            skLineSegment(sketch, "E5.90.9.0", {"start": v(-8.2, -27.77) * mm, "end": v(-8.2, -35.14) * mm});
            skLineSegment(sketch, "E5.93.9.0", {"start": v(35.24, -27.77) * mm, "end": v(35.24, -35.14) * mm});
            skLineSegment(sketch, "E5.0.10.0", {"start": v(-8.2, -36.77) * mm, "end": v(-0.83, -36.77) * mm});
            skLineSegment(sketch, "E5.3.10.0", {"start": v(0.83, -36.77) * mm, "end": v(8.2, -36.77) * mm});
            skLineSegment(sketch, "E5.6.10.0", {"start": v(18.86, -36.77) * mm, "end": v(26.23, -36.77) * mm});
            skLineSegment(sketch, "E5.9.10.0", {"start": v(-17.2, -44.13) * mm, "end": v(-9.84, -44.13) * mm});
            skLineSegment(sketch, "E5.12.10.0", {"start": v(8.2, -36.77) * mm, "end": v(8.2, -44.13) * mm});
            skLineSegment(sketch, "E5.15.10.0", {"start": v(-35.24, -44.13) * mm, "end": v(-27.88, -44.13) * mm});
            skLineSegment(sketch, "E5.18.10.0", {"start": v(-17.2, -36.77) * mm, "end": v(-17.2, -44.13) * mm});
            skLineSegment(sketch, "E5.21.10.0", {"start": v(-17.2, -36.77) * mm, "end": v(-9.84, -36.77) * mm});
            skLineSegment(sketch, "E5.24.10.0", {"start": v(-0.83, -36.77) * mm, "end": v(-0.83, -44.13) * mm});
            skLineSegment(sketch, "E5.27.10.0", {"start": v(-35.24, -36.77) * mm, "end": v(-27.88, -36.77) * mm});
            skLineSegment(sketch, "E5.30.10.0", {"start": v(27.88, -36.77) * mm, "end": v(35.24, -36.77) * mm});
            skLineSegment(sketch, "E5.33.10.0", {"start": v(-8.2, -44.13) * mm, "end": v(-0.83, -44.13) * mm});
            skLineSegment(sketch, "E5.36.10.0", {"start": v(-35.24, -36.77) * mm, "end": v(-35.24, -44.13) * mm});
            skLineSegment(sketch, "E5.39.10.0", {"start": v(-27.88, -36.77) * mm, "end": v(-27.88, -44.13) * mm});
            skLineSegment(sketch, "E5.42.10.0", {"start": v(0.83, -44.13) * mm, "end": v(8.2, -44.13) * mm});
            skLineSegment(sketch, "E5.45.10.0", {"start": v(18.86, -44.13) * mm, "end": v(26.23, -44.13) * mm});
            skLineSegment(sketch, "E5.48.10.0", {"start": v(-18.86, -36.77) * mm, "end": v(-18.86, -44.13) * mm});
            skLineSegment(sketch, "E5.51.10.0", {"start": v(-26.23, -44.13) * mm, "end": v(-18.86, -44.13) * mm});
            skLineSegment(sketch, "E5.54.10.0", {"start": v(-26.23, -36.77) * mm, "end": v(-26.23, -44.13) * mm});
            skLineSegment(sketch, "E5.57.10.0", {"start": v(-26.23, -36.77) * mm, "end": v(-18.86, -36.77) * mm});
            skLineSegment(sketch, "E5.60.10.0", {"start": v(-9.84, -36.77) * mm, "end": v(-9.84, -44.13) * mm});
            skLineSegment(sketch, "E5.63.10.0", {"start": v(9.84, -36.77) * mm, "end": v(9.84, -44.13) * mm});
            skLineSegment(sketch, "E5.66.10.0", {"start": v(9.84, -36.77) * mm, "end": v(17.2, -36.77) * mm});
            skLineSegment(sketch, "E5.69.10.0", {"start": v(17.2, -36.77) * mm, "end": v(17.2, -44.13) * mm});
            skLineSegment(sketch, "E5.72.10.0", {"start": v(27.88, -44.13) * mm, "end": v(35.24, -44.13) * mm});
            skLineSegment(sketch, "E5.75.10.0", {"start": v(0.83, -36.77) * mm, "end": v(0.83, -44.13) * mm});
            skLineSegment(sketch, "E5.78.10.0", {"start": v(18.86, -36.77) * mm, "end": v(18.86, -44.13) * mm});
            skLineSegment(sketch, "E5.81.10.0", {"start": v(27.88, -36.77) * mm, "end": v(27.88, -44.13) * mm});
            skLineSegment(sketch, "E5.84.10.0", {"start": v(9.84, -44.13) * mm, "end": v(17.2, -44.13) * mm});
            skLineSegment(sketch, "E5.87.10.0", {"start": v(26.23, -36.77) * mm, "end": v(26.23, -44.13) * mm});
            skLineSegment(sketch, "E5.90.10.0", {"start": v(-8.2, -36.77) * mm, "end": v(-8.2, -44.13) * mm});
            skLineSegment(sketch, "E5.93.10.0", {"start": v(35.24, -36.77) * mm, "end": v(35.24, -44.13) * mm});
            skLineSegment(sketch, "E5.0.11.0", {"start": v(-8.2, -45.76) * mm, "end": v(-0.83, -45.76) * mm});
            skLineSegment(sketch, "E5.3.11.0", {"start": v(0.83, -45.76) * mm, "end": v(8.2, -45.76) * mm});
            skLineSegment(sketch, "E5.6.11.0", {"start": v(18.86, -45.76) * mm, "end": v(26.23, -45.76) * mm});
            skLineSegment(sketch, "E5.9.11.0", {"start": v(-17.2, -53.12) * mm, "end": v(-9.84, -53.12) * mm});
            skLineSegment(sketch, "E5.12.11.0", {"start": v(8.2, -45.76) * mm, "end": v(8.2, -53.12) * mm});
            skLineSegment(sketch, "E5.15.11.0", {"start": v(-35.24, -53.12) * mm, "end": v(-27.88, -53.12) * mm});
            skLineSegment(sketch, "E5.18.11.0", {"start": v(-17.2, -45.76) * mm, "end": v(-17.2, -53.12) * mm});
            skLineSegment(sketch, "E5.21.11.0", {"start": v(-17.2, -45.76) * mm, "end": v(-9.84, -45.76) * mm});
            skLineSegment(sketch, "E5.24.11.0", {"start": v(-0.83, -45.76) * mm, "end": v(-0.83, -53.12) * mm});
            skLineSegment(sketch, "E5.27.11.0", {"start": v(-35.24, -45.76) * mm, "end": v(-27.88, -45.76) * mm});
            skLineSegment(sketch, "E5.30.11.0", {"start": v(27.88, -45.76) * mm, "end": v(35.24, -45.76) * mm});
            skLineSegment(sketch, "E5.33.11.0", {"start": v(-8.2, -53.12) * mm, "end": v(-0.83, -53.12) * mm});
            skLineSegment(sketch, "E5.36.11.0", {"start": v(-35.24, -45.76) * mm, "end": v(-35.24, -53.12) * mm});
            skLineSegment(sketch, "E5.39.11.0", {"start": v(-27.88, -45.76) * mm, "end": v(-27.88, -53.12) * mm});
            skLineSegment(sketch, "E5.42.11.0", {"start": v(0.83, -53.12) * mm, "end": v(8.2, -53.12) * mm});
            skLineSegment(sketch, "E5.45.11.0", {"start": v(18.86, -53.12) * mm, "end": v(26.23, -53.12) * mm});
            skLineSegment(sketch, "E5.48.11.0", {"start": v(-18.86, -45.76) * mm, "end": v(-18.86, -53.12) * mm});
            skLineSegment(sketch, "E5.51.11.0", {"start": v(-26.23, -53.12) * mm, "end": v(-18.86, -53.12) * mm});
            skLineSegment(sketch, "E5.54.11.0", {"start": v(-26.23, -45.76) * mm, "end": v(-26.23, -53.12) * mm});
            skLineSegment(sketch, "E5.57.11.0", {"start": v(-26.23, -45.76) * mm, "end": v(-18.86, -45.76) * mm});
            skLineSegment(sketch, "E5.60.11.0", {"start": v(-9.84, -45.76) * mm, "end": v(-9.84, -53.12) * mm});
            skLineSegment(sketch, "E5.63.11.0", {"start": v(9.84, -45.76) * mm, "end": v(9.84, -53.12) * mm});
            skLineSegment(sketch, "E5.66.11.0", {"start": v(9.84, -45.76) * mm, "end": v(17.2, -45.76) * mm});
            skLineSegment(sketch, "E5.69.11.0", {"start": v(17.2, -45.76) * mm, "end": v(17.2, -53.12) * mm});
            skLineSegment(sketch, "E5.72.11.0", {"start": v(27.88, -53.12) * mm, "end": v(35.24, -53.12) * mm});
            skLineSegment(sketch, "E5.75.11.0", {"start": v(0.83, -45.76) * mm, "end": v(0.83, -53.12) * mm});
            skLineSegment(sketch, "E5.78.11.0", {"start": v(18.86, -45.76) * mm, "end": v(18.86, -53.12) * mm});
            skLineSegment(sketch, "E5.81.11.0", {"start": v(27.88, -45.76) * mm, "end": v(27.88, -53.12) * mm});
            skLineSegment(sketch, "E5.84.11.0", {"start": v(9.84, -53.12) * mm, "end": v(17.2, -53.12) * mm});
            skLineSegment(sketch, "E5.87.11.0", {"start": v(26.23, -45.76) * mm, "end": v(26.23, -53.12) * mm});
            skLineSegment(sketch, "E5.90.11.0", {"start": v(-8.2, -45.76) * mm, "end": v(-8.2, -53.12) * mm});
            skLineSegment(sketch, "E5.93.11.0", {"start": v(35.24, -45.76) * mm, "end": v(35.24, -53.12) * mm});
            skSolve(sketch);
        }
        {
            var Q0;
            Q0 = qSketchRegion(id + "F0", true);
            extrude(context, id + "F1", {"entities" : qUnion([Q0]), "depth" : 4.72 * mm});
        }
        {
            var Q0;
            Q0=makeQuery(id+"F1.opExtrude","SWEPT_EDGE",EDGE,{"disambiguationData":[OSD([sQuery(id+"F0.wireOp",EDGE,"E0.bottom"),sQuery(id+"F0.wireOp",EDGE,"E0.left")])]});
            var Q1;
            Q1=makeQuery(id+"F1.opExtrude","SWEPT_EDGE",EDGE,{"disambiguationData":[OSD([sQuery(id+"F0.wireOp",EDGE,"E0.top"),sQuery(id+"F0.wireOp",EDGE,"E0.left")])]});
            var Q2;
            Q2=makeQuery(id+"F1.opExtrude","SWEPT_EDGE",EDGE,{"disambiguationData":[OSD([sQuery(id+"F0.wireOp",EDGE,"E0.top"),sQuery(id+"F0.wireOp",EDGE,"E0.right")])]});
            var Q3;
            Q3=makeQuery(id+"F1.opExtrude","SWEPT_EDGE",EDGE,{"disambiguationData":[OSD([sQuery(id+"F0.wireOp",EDGE,"E0.bottom"),sQuery(id+"F0.wireOp",EDGE,"E0.right")])]});
            fillet(context, id + "F2", {"entities" : qUnion([Q0, Q1, Q2, Q3]), "radius" : 2.54 * mm, "tangentPropagation" : true, "allowEdgeOverflow" : false});
        }
    });
